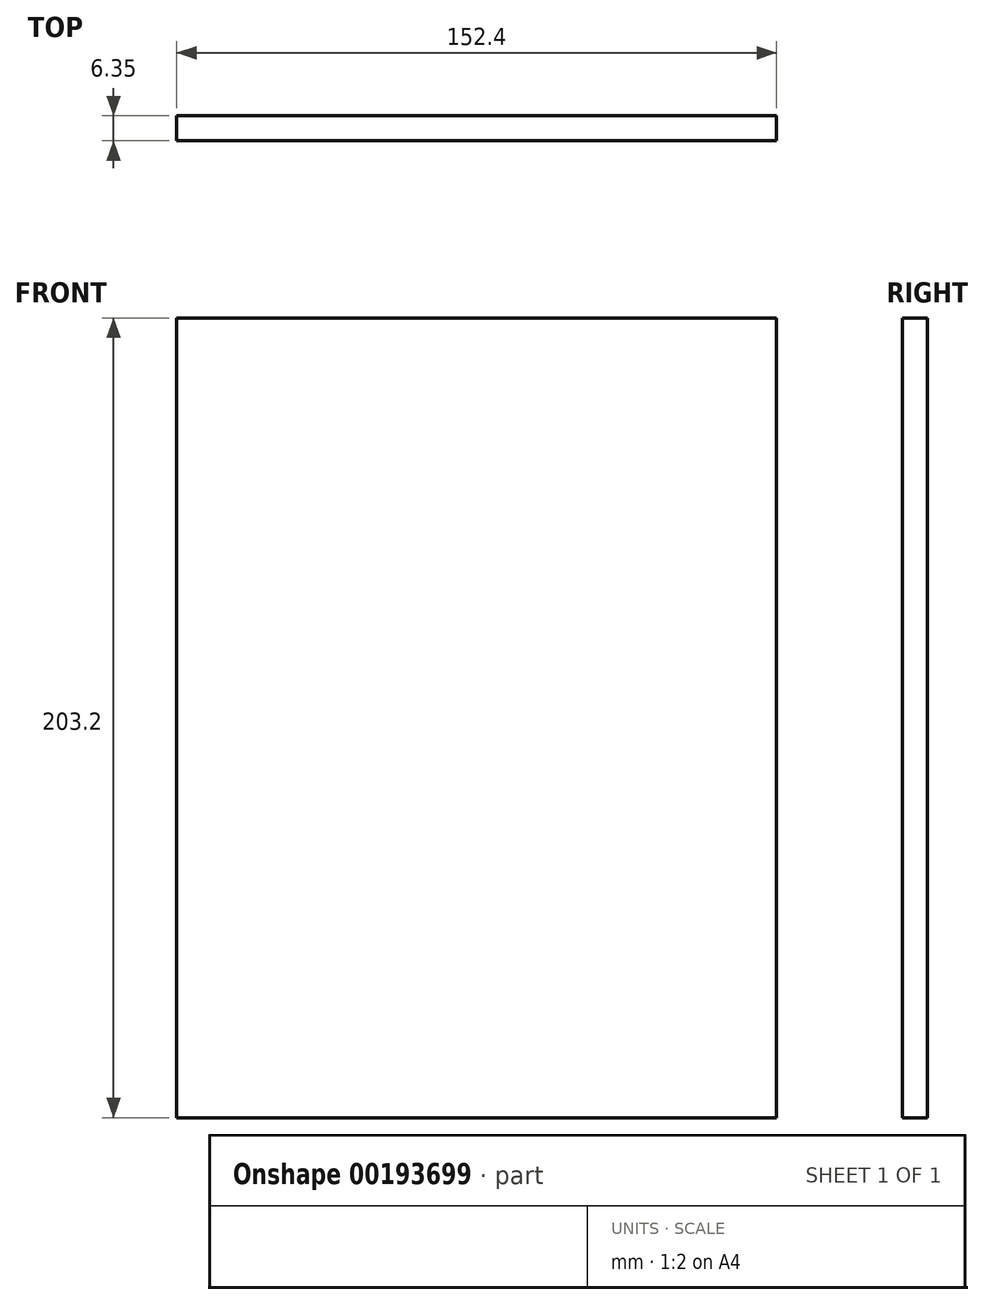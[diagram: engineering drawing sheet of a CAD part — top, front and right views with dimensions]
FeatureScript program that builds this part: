
annotation { "Feature Type Name" : "Feature", "Feature Type Description" : "" }
export const myFeature = defineFeature(function(context is Context, id is Id, definition is map)
    precondition{}
    {
        {
            var Q0;
            Q0=qCreatedBy(makeId("Front.planeOp"),FACE);
            var sketch = newSketch(context, id + "F0", { "sketchPlane" : qUnion([Q0])});
            skLineSegment(sketch, "E0.bottom", {"start": v(-76.2, 101.6) * mm, "end": v(76.2, 101.6) * mm});
            skLineSegment(sketch, "E0.top", {"start": v(-76.2, -101.6) * mm, "end": v(76.2, -101.6) * mm});
            skLineSegment(sketch, "E0.left", {"start": v(-76.2, 101.6) * mm, "end": v(-76.2, -101.6) * mm});
            skLineSegment(sketch, "E0.right", {"start": v(76.2, 101.6) * mm, "end": v(76.2, -101.6) * mm});
            skPoint(sketch, "E0.middle", {"position": v(0, 0) * mm});
            skSolve(sketch);
        }
        {
            var Q0;
            Q0=makeQuery(id+"F0.imprint","IMPRINT",FACE,{"disambiguationData":[TD([[makeQuery(id+"F0.imprint","IMPRINT",EDGE,{"derivedFrom":sQuery(id+"F0.wireOp",EDGE,"E0.bottom")}),-1.0]])]});
            extrude(context, id + "F1", {"entities" : qUnion([Q0]), "depth" : 6.35 * mm});
        }
    });
